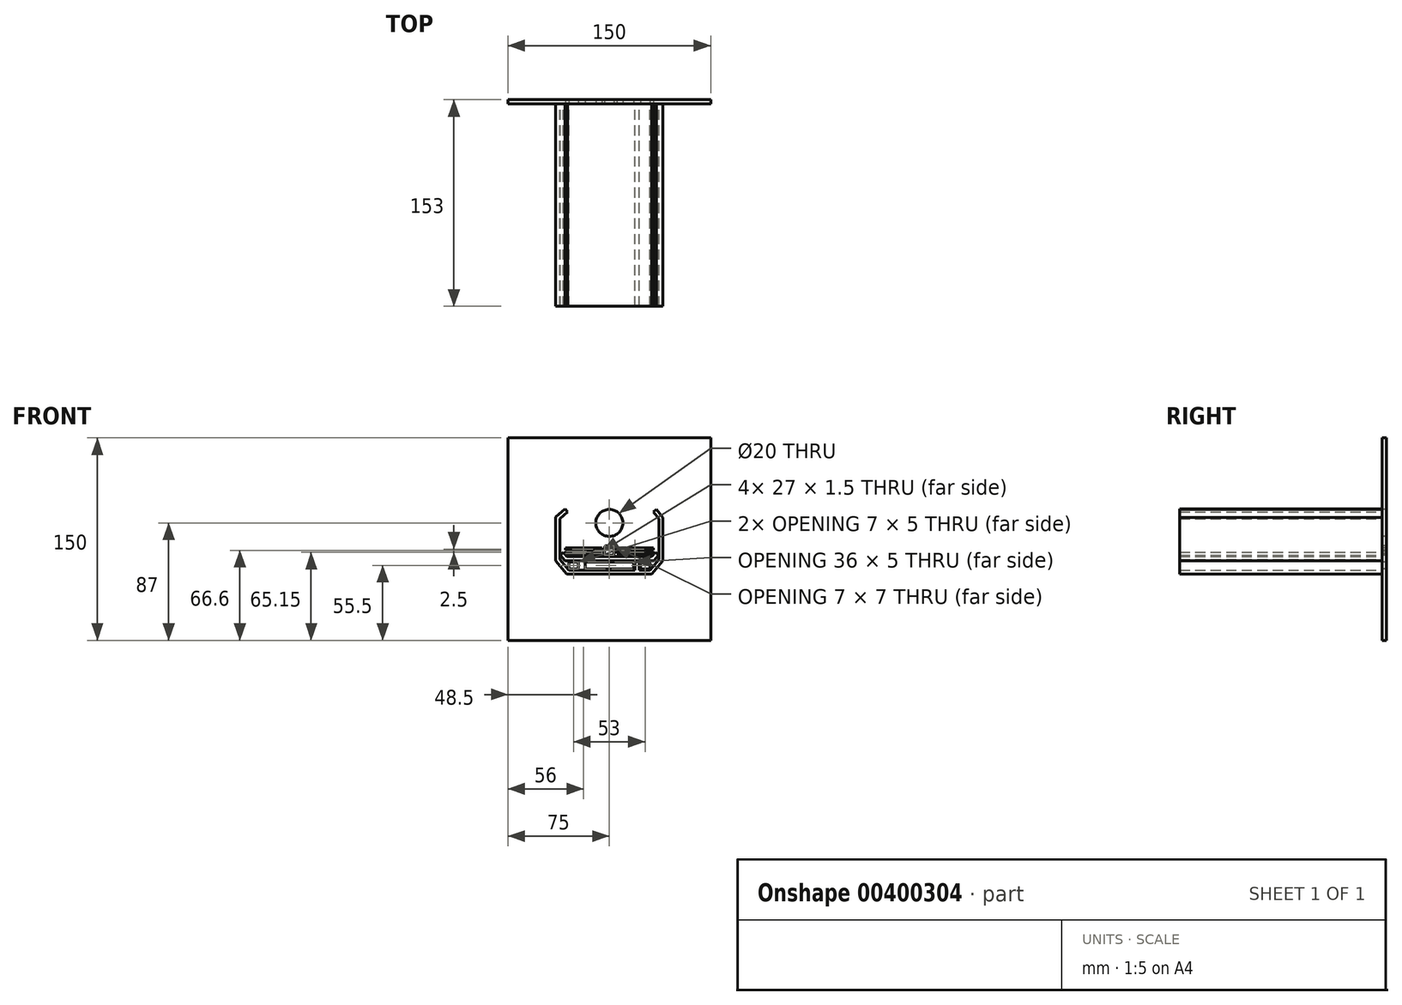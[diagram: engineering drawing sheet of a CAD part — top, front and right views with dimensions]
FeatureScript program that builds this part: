
annotation { "Feature Type Name" : "Feature", "Feature Type Description" : "" }
export const myFeature = defineFeature(function(context is Context, id is Id, definition is map)
    precondition{}
    {
        {
            var Q0;
            Q0=qCreatedBy(makeId("Front.planeOp"),FACE);
            var sketch = newSketch(context, id + "F0", { "sketchPlane" : qUnion([Q0])});
            skLineSegment(sketch, "E0.bottom", {"start": v(75, 75) * mm, "end": v(-75, 75) * mm});
            skLineSegment(sketch, "E0.top", {"start": v(75, -75) * mm, "end": v(-75, -75) * mm});
            skLineSegment(sketch, "E0.left", {"start": v(75, 75) * mm, "end": v(75, -75) * mm});
            skLineSegment(sketch, "E0.right", {"start": v(-75, 75) * mm, "end": v(-75, -75) * mm});
            skPoint(sketch, "E0.middle", {"position": v(0, 0) * mm});
            skSolve(sketch);
        }
        {
            var Q0;
            Q0=makeQuery(id+"F0.imprint","IMPRINT",FACE,{"disambiguationData":[TD([[makeQuery(id+"F0.imprint","IMPRINT",EDGE,{"derivedFrom":sQuery(id+"F0.wireOp",EDGE,"E0.bottom")}),1.0]])]});
            extrude(context, id + "F1", {"entities" : qUnion([Q0]), "depth" : 3 * mm});
        }
        {
            var Q0;
            Q0=makeQuery(id+"F1.opExtrude","CAP_FACE",FACE,{"disambiguationData":[OSD([sQuery(id+"F0.wireOp",EDGE,"E0.bottom"),sQuery(id+"F0.wireOp",EDGE,"E0.top"),sQuery(id+"F0.wireOp",EDGE,"E0.left"),sQuery(id+"F0.wireOp",EDGE,"E0.right")])],"isStart":false});
            var sketch = newSketch(context, id + "F2", { "sketchPlane" : qUnion([Q0])});
            skLineSegment(sketch, "E1", {"start": v(-30.75, 20) * mm, "end": v(-36.71, 15) * mm});
            skLineSegment(sketch, "E2", {"start": v(-36.71, 15) * mm, "end": v(-36.71, -15) * mm});
            skLineSegment(sketch, "E3", {"start": v(-36.71, -15) * mm, "end": v(-30, -23) * mm});
            skLineSegment(sketch, "E4", {"start": v(-30, -23) * mm, "end": v(30, -23) * mm});
            skLineSegment(sketch, "E5", {"start": v(30, -23) * mm, "end": v(36.71, -15) * mm});
            skLineSegment(sketch, "E6", {"start": v(36.71, -15) * mm, "end": v(36.71, 15) * mm});
            skLineSegment(sketch, "E7", {"start": v(36.71, 15) * mm, "end": v(32.52, 20) * mm});
            skCircle(sketch, "E8", {"center": v(0, 12) * mm, "radius": 10 * mm});
            skLineSegment(sketch, "E9", {"start": v(0, 0) * mm, "end": v(0, 75) * mm, "construction": true});
            skLineSegment(sketch, "E10.0", {"start": v(39.71, 16.1) * mm, "end": v(34.82, 21.93) * mm});
            skLineSegment(sketch, "E10.1", {"start": v(39.71, -16.1) * mm, "end": v(39.71, 16.1) * mm});
            skLineSegment(sketch, "E10.2", {"start": v(31.4, -26) * mm, "end": v(39.71, -16.1) * mm});
            skLineSegment(sketch, "E10.3", {"start": v(-32.68, 22.3) * mm, "end": v(-39.71, 16.4) * mm});
            skLineSegment(sketch, "E10.4", {"start": v(-39.71, 16.4) * mm, "end": v(-39.71, -16.1) * mm});
            skLineSegment(sketch, "E10.5", {"start": v(-39.71, -16.1) * mm, "end": v(-31.4, -26) * mm});
            skLineSegment(sketch, "E10.6", {"start": v(-31.4, -26) * mm, "end": v(31.4, -26) * mm});
            skLineSegment(sketch, "E11", {"start": v(-30.75, 20) * mm, "end": v(-32.68, 22.3) * mm});
            skLineSegment(sketch, "E12", {"start": v(34.82, 21.93) * mm, "end": v(32.52, 20) * mm});
            skLineSegment(sketch, "E13.bottom", {"start": v(-22, -23) * mm, "end": v(-19, -23) * mm});
            skLineSegment(sketch, "E13.top", {"start": v(-22, -16) * mm, "end": v(-19, -16) * mm});
            skLineSegment(sketch, "E13.left", {"start": v(-22, -23) * mm, "end": v(-22, -16) * mm});
            skLineSegment(sketch, "E13.right", {"start": v(-19, -23) * mm, "end": v(-19, -16) * mm});
            skLineSegment(sketch, "E14", {"start": v(-34.07, -9.84) * mm, "end": v(-31.5, -12.9) * mm});
            skLineSegment(sketch, "E15", {"start": v(-31.5, -12.9) * mm, "end": v(31.5, -12.9) * mm});
            skLineSegment(sketch, "E16", {"start": v(31.5, -12.9) * mm, "end": v(34.07, -9.84) * mm});
            skLineSegment(sketch, "E17.MirrorCS", {"start": v(22, -23) * mm, "end": v(22, -16) * mm});
            skLineSegment(sketch, "E18.MirrorCS", {"start": v(22, -16) * mm, "end": v(19, -16) * mm});
            skLineSegment(sketch, "E19.MirrorCS", {"start": v(19, -23) * mm, "end": v(19, -16) * mm});
            skLineSegment(sketch, "E20.0", {"start": v(32.9, -15.9) * mm, "end": v(36.37, -11.76) * mm});
            skLineSegment(sketch, "E20.1", {"start": v(-32.9, -15.9) * mm, "end": v(32.9, -15.9) * mm});
            skLineSegment(sketch, "E20.2", {"start": v(-36.37, -11.76) * mm, "end": v(-32.9, -15.9) * mm});
            skLineSegment(sketch, "E21", {"start": v(-34.07, -9.84) * mm, "end": v(-36.37, -11.76) * mm});
            skLineSegment(sketch, "E22", {"start": v(34.07, -9.84) * mm, "end": v(36.37, -11.76) * mm});
            skLineSegment(sketch, "E23.bottom", {"start": v(-17, -17) * mm, "end": v(17, -17) * mm});
            skLineSegment(sketch, "E23.top", {"start": v(-17, -22) * mm, "end": v(17, -22) * mm});
            skLineSegment(sketch, "E23.left", {"start": v(-18, -18) * mm, "end": v(-18, -21) * mm});
            skLineSegment(sketch, "E23.right", {"start": v(18, -18) * mm, "end": v(18, -21) * mm});
            skLineSegment(sketch, "E24.bottom", {"start": v(24, -17) * mm, "end": v(29, -17) * mm});
            skLineSegment(sketch, "E24.top", {"start": v(24, -22) * mm, "end": v(29, -22) * mm});
            skLineSegment(sketch, "E24.left", {"start": v(23, -18) * mm, "end": v(23, -21) * mm});
            skLineSegment(sketch, "E24.right", {"start": v(30, -18) * mm, "end": v(30, -21) * mm});
            skLineSegment(sketch, "E25.MirrorCS", {"start": v(-30, -18) * mm, "end": v(-30, -21) * mm});
            skLineSegment(sketch, "E26.MirrorCS", {"start": v(-23, -18) * mm, "end": v(-23, -21) * mm});
            skLineSegment(sketch, "E27.MirrorCS", {"start": v(-24, -22) * mm, "end": v(-29, -22) * mm});
            skLineSegment(sketch, "E28.MirrorCS", {"start": v(-24, -17) * mm, "end": v(-29, -17) * mm});
            skLineSegment(sketch, "E29.bottom", {"start": v(-2.5, -4.9) * mm, "end": v(2.5, -4.9) * mm});
            skLineSegment(sketch, "E29.top", {"start": v(-2.5, -11.9) * mm, "end": v(2.5, -11.9) * mm});
            skLineSegment(sketch, "E29.left", {"start": v(-3.5, -5.9) * mm, "end": v(-3.5, -10.9) * mm});
            skLineSegment(sketch, "E29.right", {"start": v(3.5, -5.9) * mm, "end": v(3.5, -10.9) * mm});
            skLineSegment(sketch, "E30.bottom", {"start": v(-32.5, -9.1) * mm, "end": v(-5.5, -9.1) * mm});
            skLineSegment(sketch, "E30.top", {"start": v(-32.5, -10.6) * mm, "end": v(-5.5, -10.6) * mm});
            skLineSegment(sketch, "E30.left", {"start": v(-32.5, -9.1) * mm, "end": v(-32.5, -10.6) * mm});
            skLineSegment(sketch, "E30.right", {"start": v(-5.5, -9.1) * mm, "end": v(-5.5, -10.6) * mm});
            skLineSegment(sketch, "E31.bottom", {"start": v(-32.5, -6.6) * mm, "end": v(-5.5, -6.6) * mm});
            skLineSegment(sketch, "E31.top", {"start": v(-32.5, -8.1) * mm, "end": v(-5.5, -8.1) * mm});
            skLineSegment(sketch, "E31.left", {"start": v(-32.5, -6.6) * mm, "end": v(-32.5, -8.1) * mm});
            skLineSegment(sketch, "E31.right", {"start": v(-5.5, -6.6) * mm, "end": v(-5.5, -8.1) * mm});
            skPoint(sketch, "E32.visualSharp", {"position": v(18, -17) * mm});
            skArc(sketch, "E32.filletArc", {"start": v(18, -18) * mm, "mid": v(17.7, -17.3) * mm, "end": v(17, -17) * mm});
            skPoint(sketch, "E33.visualSharp", {"position": v(18, -22) * mm});
            skArc(sketch, "E33.filletArc", {"start": v(17, -22) * mm, "mid": v(17.7, -21.7) * mm, "end": v(18, -21) * mm});
            skPoint(sketch, "E34.visualSharp", {"position": v(-18, -22) * mm});
            skArc(sketch, "E34.filletArc", {"start": v(-18, -21) * mm, "mid": v(-17.7, -21.7) * mm, "end": v(-17, -22) * mm});
            skPoint(sketch, "E35.visualSharp", {"position": v(-18, -17) * mm});
            skArc(sketch, "E35.filletArc", {"start": v(-17, -17) * mm, "mid": v(-17.7, -17.3) * mm, "end": v(-18, -18) * mm});
            skPoint(sketch, "E36.visualSharp", {"position": v(-23, -17) * mm});
            skArc(sketch, "E36.filletArc", {"start": v(-23, -18) * mm, "mid": v(-23.3, -17.3) * mm, "end": v(-24, -17) * mm});
            skPoint(sketch, "E37.visualSharp", {"position": v(-30, -17) * mm});
            skArc(sketch, "E37.filletArc", {"start": v(-29, -17) * mm, "mid": v(-29.7, -17.3) * mm, "end": v(-30, -18) * mm});
            skPoint(sketch, "E38.visualSharp", {"position": v(-30, -22) * mm});
            skArc(sketch, "E38.filletArc", {"start": v(-30, -21) * mm, "mid": v(-29.7, -21.7) * mm, "end": v(-29, -22) * mm});
            skPoint(sketch, "E39.visualSharp", {"position": v(-23, -22) * mm});
            skArc(sketch, "E39.filletArc", {"start": v(-24, -22) * mm, "mid": v(-23.3, -21.7) * mm, "end": v(-23, -21) * mm});
            skPoint(sketch, "E40.visualSharp", {"position": v(23, -17) * mm});
            skArc(sketch, "E40.filletArc", {"start": v(24, -17) * mm, "mid": v(23.3, -17.3) * mm, "end": v(23, -18) * mm});
            skPoint(sketch, "E41.visualSharp", {"position": v(30, -22) * mm});
            skArc(sketch, "E41.filletArc", {"start": v(29, -22) * mm, "mid": v(29.7, -21.7) * mm, "end": v(30, -21) * mm});
            skPoint(sketch, "E42.visualSharp", {"position": v(23, -22) * mm});
            skArc(sketch, "E42.filletArc", {"start": v(23, -21) * mm, "mid": v(23.3, -21.7) * mm, "end": v(24, -22) * mm});
            skPoint(sketch, "E43.visualSharp", {"position": v(30, -17) * mm});
            skArc(sketch, "E43.filletArc", {"start": v(30, -18) * mm, "mid": v(29.7, -17.3) * mm, "end": v(29, -17) * mm});
            skPoint(sketch, "E44.visualSharp", {"position": v(-3.5, -4.9) * mm});
            skArc(sketch, "E44.filletArc", {"start": v(-2.5, -4.9) * mm, "mid": v(-3.2, -5.2) * mm, "end": v(-3.5, -5.9) * mm});
            skPoint(sketch, "E45.visualSharp", {"position": v(3.5, -11.9) * mm});
            skArc(sketch, "E45.filletArc", {"start": v(2.5, -11.9) * mm, "mid": v(3.2, -11.6) * mm, "end": v(3.5, -10.9) * mm});
            skPoint(sketch, "E46.visualSharp", {"position": v(3.5, -4.9) * mm});
            skArc(sketch, "E46.filletArc", {"start": v(3.5, -5.9) * mm, "mid": v(3.2, -5.2) * mm, "end": v(2.5, -4.9) * mm});
            skPoint(sketch, "E47.visualSharp", {"position": v(-3.5, -11.9) * mm});
            skArc(sketch, "E47.filletArc", {"start": v(-3.5, -10.9) * mm, "mid": v(-3.2, -11.6) * mm, "end": v(-2.5, -11.9) * mm});
            skLineSegment(sketch, "E48.MirrorCS", {"start": v(5.5, -9.1) * mm, "end": v(5.5, -10.6) * mm});
            skLineSegment(sketch, "E49.MirrorCS", {"start": v(32.5, -9.1) * mm, "end": v(32.5, -10.6) * mm});
            skLineSegment(sketch, "E50.MirrorCS", {"start": v(32.5, -6.6) * mm, "end": v(32.5, -8.1) * mm});
            skLineSegment(sketch, "E51.MirrorCS", {"start": v(5.5, -6.6) * mm, "end": v(5.5, -8.1) * mm});
            skLineSegment(sketch, "E52.MirrorCS", {"start": v(32.5, -10.6) * mm, "end": v(5.5, -10.6) * mm});
            skLineSegment(sketch, "E53.MirrorCS", {"start": v(32.5, -6.6) * mm, "end": v(5.5, -6.6) * mm});
            skLineSegment(sketch, "E54.MirrorCS", {"start": v(32.5, -8.1) * mm, "end": v(5.5, -8.1) * mm});
            skLineSegment(sketch, "E55.MirrorCS", {"start": v(32.5, -9.1) * mm, "end": v(5.5, -9.1) * mm});
            skSolve(sketch);
        }
        {
            var Q0;
            Q0=makeQuery(id+"F2.imprint","IMPRINT",FACE,{"disambiguationData":[TD([[makeQuery(id+"F2.imprint","IMPRINT",EDGE,{"derivedFrom":sQuery(id+"F2.wireOp",EDGE,"E1")}),-1.0]])]});
            var Q1;
            Q1=makeQuery(id+"F2.imprint","IMPRINT",FACE,{"disambiguationData":[TD([[makeQuery(id+"F2.imprint","IMPRINT",EDGE,{"derivedFrom":sQuery(id+"F2.wireOp",EDGE,"E13.bottom")}),1.0]])]});
            var Q2;
            Q2=makeQuery(id+"F2.imprint","IMPRINT",FACE,{"disambiguationData":[TD([[makeQuery(id+"F2.imprint","IMPRINT",EDGE,{"derivedFrom":sQuery(id+"F2.wireOp",EDGE,"E14")}),-1.0]])]});
            var Q3;
            {var subQ0=sQuery(id+"F2.wireOp",EDGE,"E17.MirrorCS");Q3=makeQuery(id+"F2.imprint","IMPRINT",FACE,{"disambiguationData":[TD([[makeQuery(id+"F2.imprint","IMPRINT",EDGE,{"derivedFrom":subQ0}),1.0]])]});}
            extrude(context, id + "F3", {"entities" : qUnion([Q0, Q1, Q2, Q3]), "operationType" : NewBodyOperationType.ADD, "depth" : 150 * mm});
        }
        {
            var Q0;
            Q0=makeQuery(id+"F2.imprint","IMPRINT",FACE,{"disambiguationData":[TD([[makeQuery(id+"F2.imprint","IMPRINT",EDGE,{"derivedFrom":sQuery(id+"F2.wireOp",EDGE,"E8")}),1.0]])]});
            var Q1;
            Q1=makeQuery(id+"F2.imprint","IMPRINT",FACE,{"disambiguationData":[TD([[makeQuery(id+"F2.imprint","IMPRINT",EDGE,{"derivedFrom":sQuery(id+"F2.wireOp",EDGE,"E25.MirrorCS")}),1.0]])]});
            var Q2;
            Q2=makeQuery(id+"F2.imprint","IMPRINT",FACE,{"disambiguationData":[TD([[makeQuery(id+"F2.imprint","IMPRINT",EDGE,{"derivedFrom":sQuery(id+"F2.wireOp",EDGE,"E23.bottom")}),-1.0]])]});
            var Q3;
            Q3=makeQuery(id+"F2.imprint","IMPRINT",FACE,{"disambiguationData":[TD([[makeQuery(id+"F2.imprint","IMPRINT",EDGE,{"derivedFrom":sQuery(id+"F2.wireOp",EDGE,"E24.bottom")}),-1.0]])]});
            var Q4;
            Q4=makeQuery(id+"F2.imprint","IMPRINT",FACE,{"disambiguationData":[TD([[makeQuery(id+"F2.imprint","IMPRINT",EDGE,{"derivedFrom":sQuery(id+"F2.wireOp",EDGE,"E29.bottom")}),-1.0]])]});
            var Q5;
            Q5=makeQuery(id+"F2.imprint","IMPRINT",FACE,{"disambiguationData":[TD([[makeQuery(id+"F2.imprint","IMPRINT",EDGE,{"derivedFrom":sQuery(id+"F2.wireOp",EDGE,"E31.bottom")}),-1.0]])]});
            var Q6;
            Q6=makeQuery(id+"F2.imprint","IMPRINT",FACE,{"disambiguationData":[TD([[makeQuery(id+"F2.imprint","IMPRINT",EDGE,{"derivedFrom":sQuery(id+"F2.wireOp",EDGE,"E30.bottom")}),-1.0]])]});
            var Q7;
            Q7=makeQuery(id+"F2.imprint","IMPRINT",FACE,{"disambiguationData":[TD([[makeQuery(id+"F2.imprint","IMPRINT",EDGE,{"derivedFrom":sQuery(id+"F2.wireOp",EDGE,"E50.MirrorCS")}),-1.0]])]});
            var Q8;
            Q8=makeQuery(id+"F2.imprint","IMPRINT",FACE,{"disambiguationData":[TD([[makeQuery(id+"F2.imprint","IMPRINT",EDGE,{"derivedFrom":sQuery(id+"F2.wireOp",EDGE,"E48.MirrorCS")}),1.0]])]});
            extrude(context, id + "F4", {"entities" : qUnion([Q0, Q1, Q2, Q3, Q4, Q5, Q6, Q7, Q8]), "operationType" : NewBodyOperationType.REMOVE, "endBound" : BoundingType.THROUGH_ALL, "oppositeDirection" : true, "depth" : 25 * mm});
        }
    });
